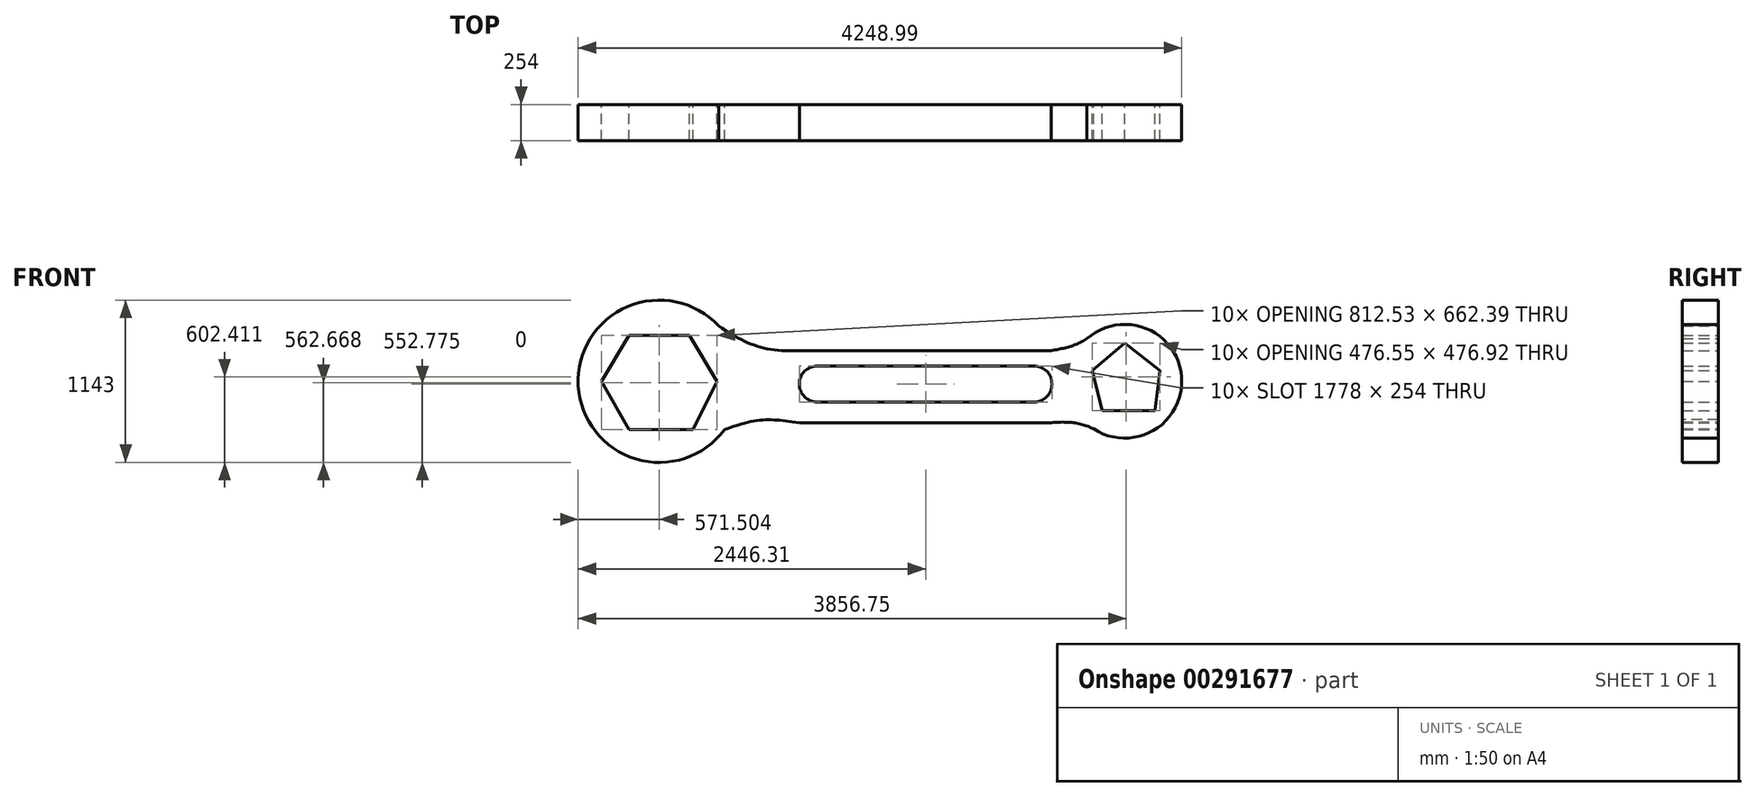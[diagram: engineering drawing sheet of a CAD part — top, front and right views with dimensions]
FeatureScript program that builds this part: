
annotation { "Feature Type Name" : "Feature", "Feature Type Description" : "" }
export const myFeature = defineFeature(function(context is Context, id is Id, definition is map)
    precondition{}
    {
        {
            var Q0;
            Q0=qCreatedBy(makeId("Front.planeOp"),FACE);
            var sketch = newSketch(context, id + "F0", { "sketchPlane" : qUnion([Q0])});
            skLineSegment(sketch, "E0", {"start": v(1731.03, 269.37) * mm, "end": v(1501.4, 75.07) * mm});
            skLineSegment(sketch, "E1", {"start": v(-1333.6, 322.36) * mm, "end": v(-1139.3, 0) * mm});
            skLineSegment(sketch, "E2", {"start": v(-1139.3, 0) * mm, "end": v(-1307.1, -340.02) * mm});
            skLineSegment(sketch, "E3", {"start": v(-1307.1, -340.02) * mm, "end": v(-1757.53, -340.02) * mm});
            skLineSegment(sketch, "E4", {"start": v(-1333.6, 322.36) * mm, "end": v(-1757.53, 322.36) * mm});
            skLineSegment(sketch, "E5", {"start": v(-1757.53, 322.36) * mm, "end": v(-1951.83, 0) * mm});
            skLineSegment(sketch, "E6", {"start": v(-1951.83, 0) * mm, "end": v(-1757.53, -340.02) * mm});
            skLineSegment(sketch, "E7", {"start": v(-432.76, 108.28) * mm, "end": v(1091.24, 108.28) * mm});
            skLineSegment(sketch, "E8", {"start": v(-432.76, -145.72) * mm, "end": v(1091.24, -145.72) * mm});
            skArc(sketch, "E9", {"start": v(-432.76, 108.28) * mm, "mid": v(-559.76, -18.72) * mm, "end": v(-432.76, -145.72) * mm});
            skArc(sketch, "E10", {"start": v(1091.24, -145.72) * mm, "mid": v(1218.24, -18.72) * mm, "end": v(1091.24, 108.28) * mm});
            skPoint(sketch, "E11.startSnap0", {"position": v(-559.76, -18.72) * mm});
            skPoint(sketch, "E11.endSnap0", {"position": v(1218.24, -18.72) * mm});
            skLineSegment(sketch, "E12", {"start": v(1501.4, 75.07) * mm, "end": v(1572.06, -207.55) * mm});
            skLineSegment(sketch, "E13", {"start": v(1943, -207.55) * mm, "end": v(1572.06, -207.55) * mm});
            skCircle(sketch, "E14", {"center": v(-1545.57, 0) * mm, "radius": 571.5 * mm});
            skPoint(sketch, "E14.centerSnap0", {"position": v(-1545.57, 322.36) * mm});
            skCircle(sketch, "E15", {"center": v(1731.03, 0) * mm, "radius": 400.88 * mm});
            skLineSegment(sketch, "E16", {"start": v(-559.76, 216.43) * mm, "end": v(1211.27, 216.43) * mm});
            skLineSegment(sketch, "E17", {"start": v(-559.76, -291.57) * mm, "end": v(1211.27, -291.57) * mm});
            skFitSpline(sketch, "E18", {"points": [v(-559.76, 216.43) * mm, v(-1126.98, 389.1) * mm], "startDerivative": vector(-758.67, -42.38) * mm, "endDerivative": vector(-548.2, 367.73) * mm});
            skFitSpline(sketch, "E19", {"points": [v(-559.76, -291.57) * mm, v(-1087.14, -341.26) * mm], "startDerivative": vector(-604.62, 75.32) * mm, "endDerivative": vector(-737, -281) * mm});
            skFitSpline(sketch, "E20", {"points": [v(1211.27, -291.57) * mm, v(1510.68, -334.89) * mm], "startDerivative": vector(406.06, 31) * mm, "endDerivative": vector(280.5, -131.97) * mm});
            skLineSegment(sketch, "E21", {"start": v(1731.03, 269.37) * mm, "end": v(1977.96, 75.07) * mm});
            skLineSegment(sketch, "E22", {"start": v(1977.96, 75.07) * mm, "end": v(1943, -207.55) * mm});
            skFitSpline(sketch, "E23", {"points": [v(1211.27, 216.43) * mm, v(1510.68, 334.89) * mm], "startDerivative": vector(371.62, 56.65) * mm, "endDerivative": vector(250.24, 219.88) * mm});
            skSolve(sketch);
        }
        {
            var Q0;
            Q0 = qSketchRegion(id + "F0", true);
            extrude(context, id + "F1", {"entities" : qUnion([Q0]), "depth" : 254 * mm});
        }
    });
